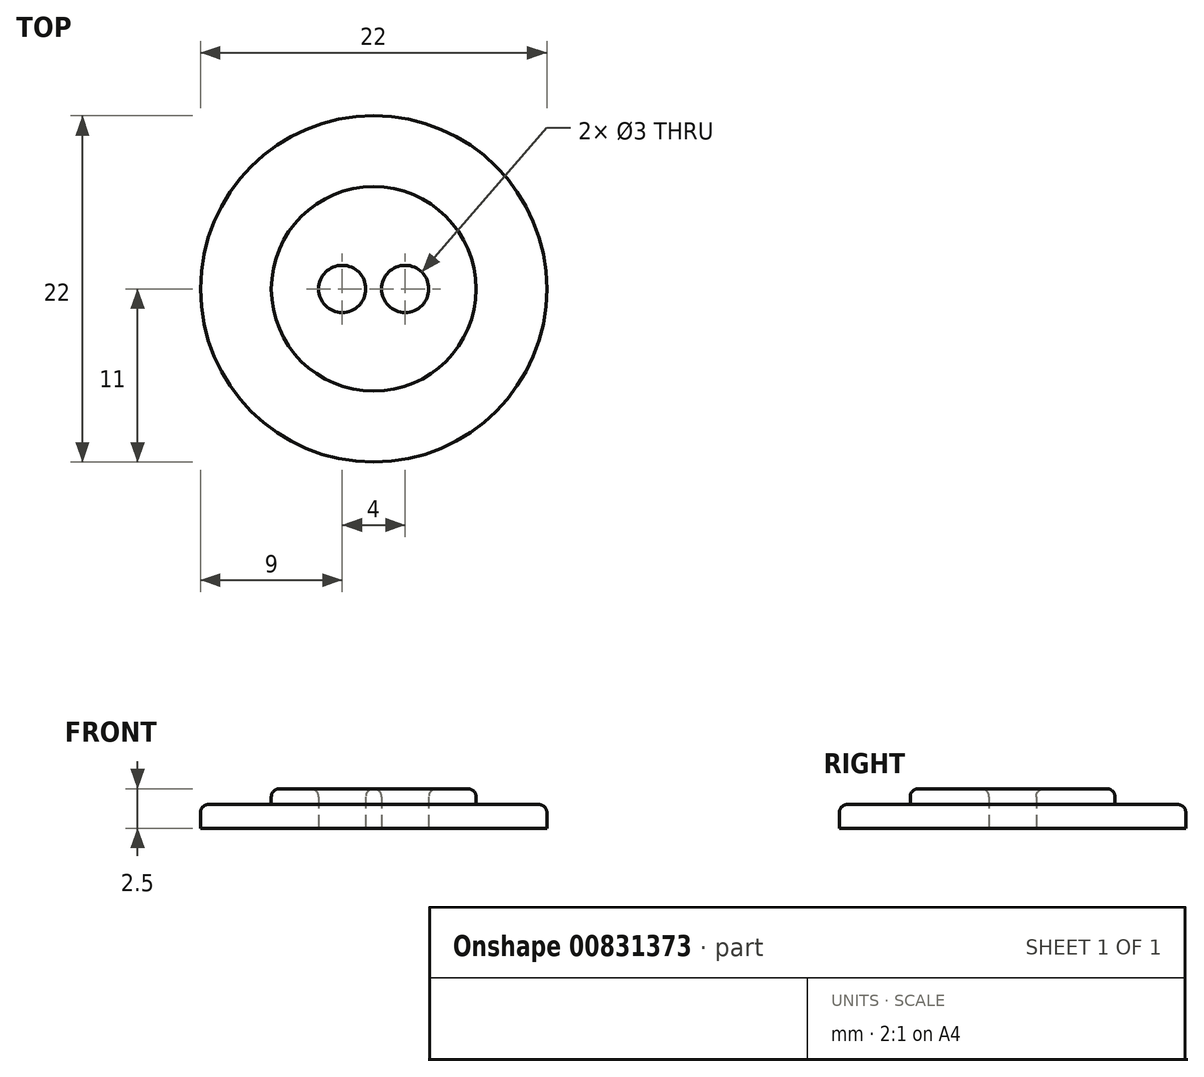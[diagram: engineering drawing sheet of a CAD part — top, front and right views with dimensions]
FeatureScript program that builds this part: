
annotation { "Feature Type Name" : "Feature", "Feature Type Description" : "" }
export const myFeature = defineFeature(function(context is Context, id is Id, definition is map)
    precondition{}
    {
        {
            var Q0;
            Q0=qCreatedBy(makeId("Top.planeOp"),FACE);
            var sketch = newSketch(context, id + "F0", { "sketchPlane" : qUnion([Q0])});
            skCircle(sketch, "E0", {"center": v(0, 0) * mm, "radius": 11 * mm});
            skCircle(sketch, "E1", {"center": v(0, 0) * mm, "radius": 6.5 * mm});
            skCircle(sketch, "E2", {"center": v(2, 0) * mm, "radius": 1.5 * mm});
            skCircle(sketch, "E3", {"center": v(-2, 0) * mm, "radius": 1.5 * mm});
            skSolve(sketch);
        }
        {
            var Q0;
            Q0=makeQuery(id+"F0.imprint","IMPRINT",FACE,{"disambiguationData":[TD([[makeQuery(id+"F0.imprint","IMPRINT",EDGE,{"derivedFrom":sQuery(id+"F0.wireOp",EDGE,"E0")}),1.0]])]});
            extrude(context, id + "F1", {"entities" : qUnion([Q0]), "depth" : 1.5 * mm, "offsetDistance" : 25 * mm});
        }
        {
            var Q0;
            Q0=makeQuery(id+"F0.imprint","IMPRINT",FACE,{"disambiguationData":[TD([[makeQuery(id+"F0.imprint","IMPRINT",EDGE,{"derivedFrom":sQuery(id+"F0.wireOp",EDGE,"E1")}),1.0]])]});
            extrude(context, id + "F2", {"entities" : qUnion([Q0]), "operationType" : NewBodyOperationType.ADD, "depth" : 2.5 * mm, "offsetDistance" : 25 * mm});
        }
        {
            var Q0;
            Q0=makeQuery(id+"F1.opExtrude","CAP_EDGE",EDGE,{"disambiguationData":[OSD([sQuery(id+"F0.wireOp",EDGE,"E0")])],"isStart":false});
            var Q1;
            Q1=makeQuery(id+"F1.opExtrude","CAP_EDGE",EDGE,{"disambiguationData":[OSD([sQuery(id+"F0.wireOp",EDGE,"E1")])],"isStart":false});
            var Q2;
            Q2=makeQuery(id+"F2.opExtrude","CAP_EDGE",EDGE,{"disambiguationData":[OSD([sQuery(id+"F0.wireOp",EDGE,"E1")])],"isStart":false});
            var Q3;
            Q3=makeQuery(id+"F2.opExtrude","CAP_EDGE",EDGE,{"disambiguationData":[OSD([sQuery(id+"F0.wireOp",EDGE,"E2")])],"isStart":false});
            var Q4;
            Q4=makeQuery(id+"F2.opExtrude","CAP_EDGE",EDGE,{"disambiguationData":[OSD([sQuery(id+"F0.wireOp",EDGE,"E3")])],"isStart":false});
            fillet(context, id + "F3", {"entities" : qUnion([Q0, Q1, Q2, Q3, Q4]), "radius" : 0.5 * mm, "tangentPropagation" : true, "allowEdgeOverflow" : false});
        }
    });
